# Revit family: HAR2430XXXX-Single
name_source: partatom
category: Furniture
units: mm (PartAtom-declared; Revit-internal decimal feet)

## family parameters
Always vertical = Yes
Cut with Voids When Loaded = No
Enable Cutting in Views = No
OmniClass Number = 23.40.20.00
OmniClass Title = General Furniture and Specialties
Render Appearance Source = Family Geometry
Room Calculation Point = No
Shared = No
Work Plane-Based = No

## types (14) — shared parameters
Default Elevation = 0"
Low Emitting Finish = Yes
Low Emitting Material = Yes
Manufacturer = Palmer Hamilton
Product Documentation Link = https://palmerhamilton.com
Salvage or Reuse = Yes
Type Comments = Harmony
URL = https://palmerhamilton.com
zero-valued in all types: Cost, Percentage of Recycled Content

## per-type parameters (varying)
| type | C WT | Description | FT 3CP | Front Panel L | Grommet L | Length | S WT | Width |
| HAR24302436 | No | Harmony, Single-Sided Table, 24WX36L | No | 29 1/4" | 9" | 36" | No | 24" |
| HAR24302442 | No | Harmony, Single-Sided Table, 24WX42L | No | 35 1/4" | 10 1/2" | 42" | No | 24" |
| HAR24302448 | No | Harmony, Single-Sided Table, 24WX48L | No | 41 1/4" | 12" | 48" | No | 24" |
| HAR24302460 | Yes | Harmony, Single-Sided Table, 24WX60L | Yes | 53 1/4" | 15" | 60" | No | 24" |
| HAR24302472 | Yes | Harmony, Single-Sided Table, 24WX72L | Yes | 65 1/4" | 18" | 72" | No | 24" |
| HAR24302484 | Yes | Harmony, Single-Sided Table, 24WX84L | Yes | 77 1/4" | 14" | 84" | Yes | 24" |
| HAR24302496 | Yes | Harmony, Single-Sided Table, 24WX96L | Yes | 89 1/4" | 16" | 96" | Yes | 24" |
| HAR24303036 | No | Harmony, Single-Sided Table, 30WX36L | No | 29 1/4" | 9" | 36" | No | 30" |
| HAR24303042 | No | Harmony, Single-Sided Table, 30WX42L | No | 35 1/4" | 10 1/2" | 42" | No | 30" |
| HAR24303048 | No | Harmony, Single-Sided Table, 30WX48L | No | 41 1/4" | 12" | 48" | No | 30" |
| HAR24303060 | Yes | Harmony, Single-Sided Table, 30WX60L | Yes | 53 1/4" | 15" | 60" | No | 30" |
| HAR24303072 | Yes | Harmony, Single-Sided Table, 30WX72L | Yes | 65 1/4" | 18" | 72" | No | 30" |
| HAR24303084 | Yes | Harmony, Single-Sided Table, 30WX84L | Yes | 77 1/4" | 14" | 84" | Yes | 30" |
| HAR24303096 | Yes | Harmony, Single-Sided Table, 30WX96L | Yes | 89 1/4" | 16" | 96" | Yes | 30" |

note: column(s) folded — value = type name in every type: Model

## geometry (parser evidence)
native form markers: Sweep x75
no freeform markers — native parametric forms only
